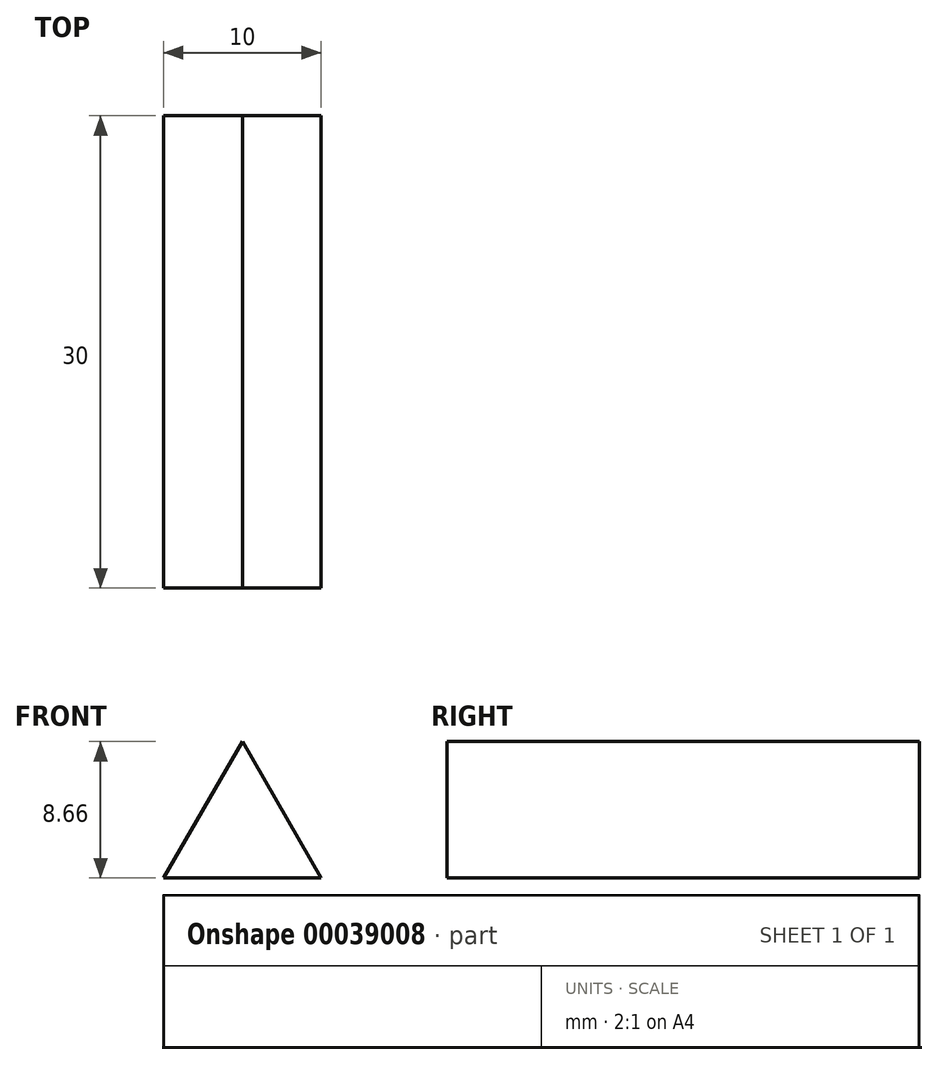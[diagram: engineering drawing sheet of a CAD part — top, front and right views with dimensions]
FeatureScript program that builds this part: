
annotation { "Feature Type Name" : "Feature", "Feature Type Description" : "" }
export const myFeature = defineFeature(function(context is Context, id is Id, definition is map)
    precondition{}
    {
        {
            var Q0;
            Q0=qCreatedBy(makeId("Front.planeOp"),FACE);
            var sketch = newSketch(context, id + "F0", { "sketchPlane" : qUnion([Q0])});
            skLineSegment(sketch, "E0", {"start": v(0, 8.66) * mm, "end": v(-5, 0) * mm});
            skLineSegment(sketch, "E1", {"start": v(-5, 0) * mm, "end": v(5, 0) * mm});
            skLineSegment(sketch, "E2", {"start": v(5, 0) * mm, "end": v(0, 8.66) * mm});
            skSolve(sketch);
        }
        {
            var Q0;
            Q0=makeQuery(id+"F0.imprint","IMPRINT",FACE,{"disambiguationData":[TD([[makeQuery(id+"F0.imprint","IMPRINT",EDGE,{"derivedFrom":sQuery(id+"F0.wireOp",EDGE,"E0")}),1.0]])]});
            extrude(context, id + "F1", {"entities" : qUnion([Q0]), "depth" : 30 * mm});
        }
    });
